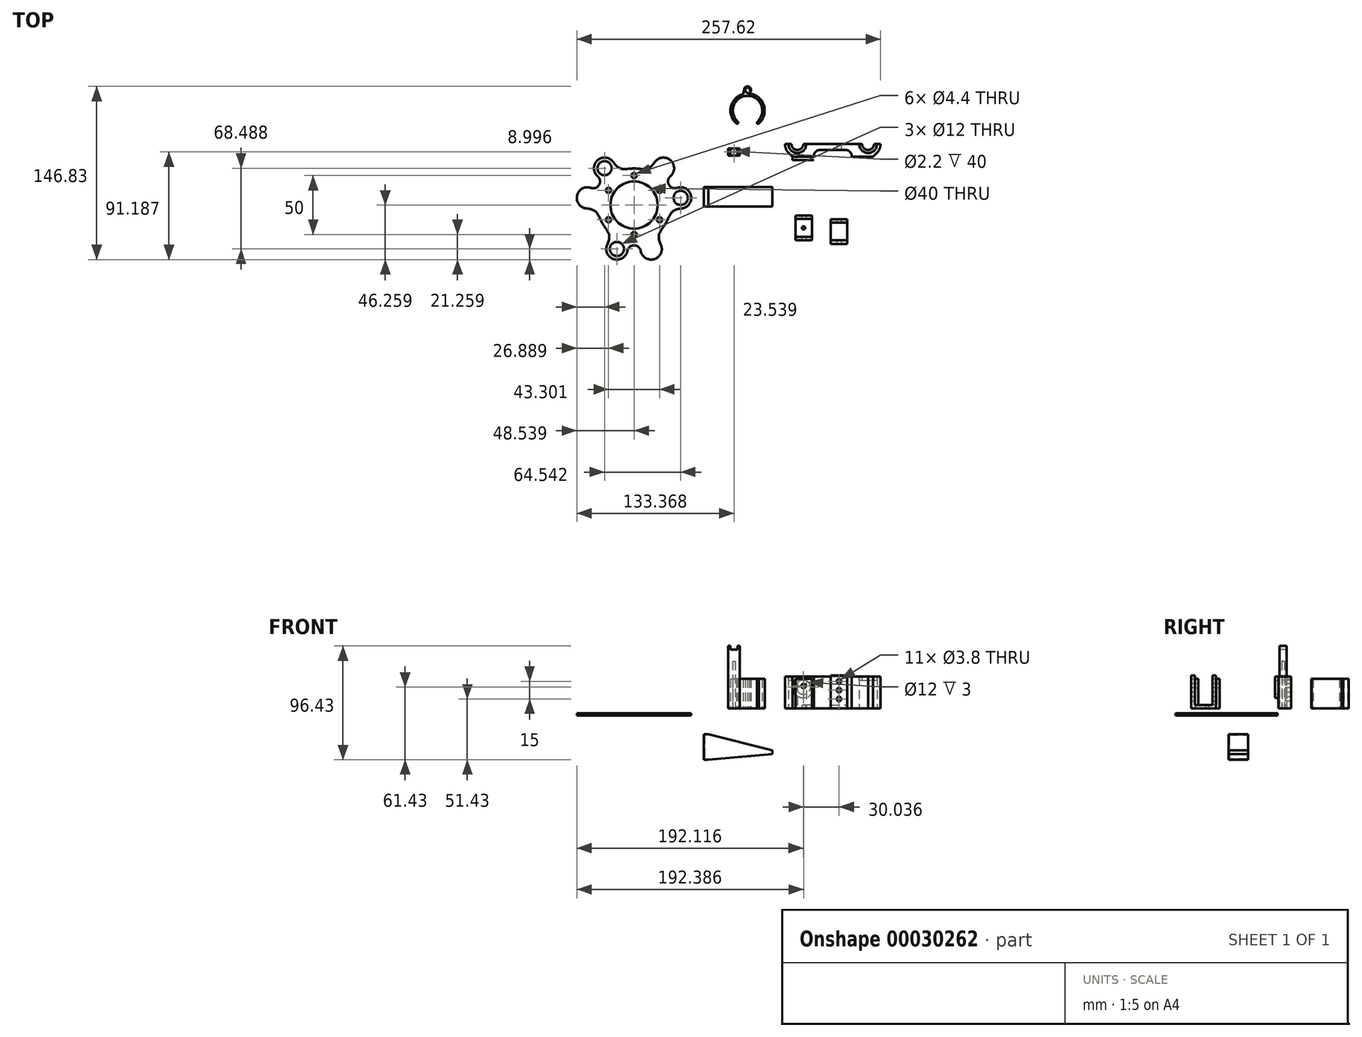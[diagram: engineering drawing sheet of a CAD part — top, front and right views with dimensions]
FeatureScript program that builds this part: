
annotation { "Feature Type Name" : "Feature", "Feature Type Description" : "" }
export const myFeature = defineFeature(function(context is Context, id is Id, definition is map)
    precondition{}
    {
        {
            var Q0;
            Q0=qCreatedBy(makeId("Top.planeOp"),FACE);
            var sketch = newSketch(context, id + "F0", { "sketchPlane" : qUnion([Q0])});
            skLineSegment(sketch, "E0.bottom", {"start": v(-40.53, 32.69) * mm, "end": v(-30.53, 32.69) * mm});
            skLineSegment(sketch, "E0.top", {"start": v(-40.53, 26.69) * mm, "end": v(-30.53, 26.69) * mm});
            skLineSegment(sketch, "E0.left", {"start": v(-40.53, 32.69) * mm, "end": v(-40.53, 26.69) * mm});
            skLineSegment(sketch, "E0.right", {"start": v(-30.53, 32.69) * mm, "end": v(-30.53, 26.69) * mm});
            skSolve(sketch);
        }
        {
            var Q0;
            Q0=makeQuery(id+"F0.imprint","IMPRINT",FACE,{"disambiguationData":[TD([[makeQuery(id+"F0.imprint","IMPRINT",EDGE,{"derivedFrom":sQuery(id+"F0.wireOp",EDGE,"E0.bottom")}),-1.0]])]});
            extrude(context, id + "F1", {"entities" : qUnion([Q0]), "depth" : 53 * mm});
        }
        {
            var Q0;
            Q0=makeQuery(id+"F1.opExtrude","CAP_FACE",FACE,{"disambiguationData":[OSD([sQuery(id+"F0.wireOp",EDGE,"E0.bottom"),sQuery(id+"F0.wireOp",EDGE,"E0.top"),sQuery(id+"F0.wireOp",EDGE,"E0.left"),sQuery(id+"F0.wireOp",EDGE,"E0.right")])],"isStart":false});
            var sketch = newSketch(context, id + "F2", { "sketchPlane" : qUnion([Q0])});
            skLineSegment(sketch, "E1", {"start": v(-38.53, 32.69) * mm, "end": v(-38.53, 26.69) * mm});
            skLineSegment(sketch, "E2", {"start": v(-32.53, 32.69) * mm, "end": v(-32.53, 26.69) * mm});
            skLineSegment(sketch, "E3", {"start": v(-38.53, 32.69) * mm, "end": v(-32.53, 32.69) * mm});
            skLineSegment(sketch, "E4", {"start": v(-38.53, 26.69) * mm, "end": v(-32.53, 26.69) * mm});
            skLineSegment(sketch, "E5", {"start": v(-38.53, 26.69) * mm, "end": v(-40.53, 26.69) * mm});
            skSolve(sketch);
        }
        {
            var Q0;
            Q0 = qSketchRegion(id + "F2", true);
            extrude(context, id + "F3", {"entities" : qUnion([Q0]), "operationType" : NewBodyOperationType.REMOVE, "oppositeDirection" : true, "depth" : 3 * mm});
        }
        {
            var Q0;
            Q0=makeQuery(id+"F1.opExtrude","CAP_FACE",FACE,{"disambiguationData":[OSD([sQuery(id+"F0.wireOp",EDGE,"E0.bottom"),sQuery(id+"F0.wireOp",EDGE,"E0.top"),sQuery(id+"F0.wireOp",EDGE,"E0.left"),sQuery(id+"F0.wireOp",EDGE,"E0.right")])],"isStart":true});
            var sketch = newSketch(context, id + "F4", { "sketchPlane" : qUnion([Q0])});
            skLineSegment(sketch, "E6", {"start": v(-35.53, -26.69) * mm, "end": v(-35.53, -32.69) * mm, "construction": true});
            skLineSegment(sketch, "E7", {"start": v(-40.53, -29.69) * mm, "end": v(-30.53, -29.69) * mm, "construction": true});
            skCircle(sketch, "E8", {"center": v(-35.53, -29.69) * mm, "radius": 1.1 * mm});
            skSolve(sketch);
        }
        {
            var Q0;
            Q0 = qSketchRegion(id + "F4", true);
            extrude(context, id + "F5", {"entities" : qUnion([Q0]), "operationType" : NewBodyOperationType.REMOVE, "oppositeDirection" : true, "depth" : 40 * mm});
        }
        {
            var Q0;
            Q0=qCreatedBy(makeId("Top.planeOp"),FACE);
            var sketch = newSketch(context, id + "F6", { "sketchPlane" : qUnion([Q0])});
            skLineSegment(sketch, "E9", {"start": v(-120.36, -15.24) * mm, "end": v(-120.36, 37.75) * mm, "construction": true});
            skLineSegment(sketch, "E10", {"start": v(-120.36, -15.24) * mm, "end": v(-160.35, -38.33) * mm, "construction": true});
            skLineSegment(sketch, "E11", {"start": v(-120.36, -15.24) * mm, "end": v(-52.6, -54.36) * mm, "construction": true});
            skLineSegment(sketch, "E12.0", {"start": v(-120.36, 13.63) * mm, "end": v(-172.85, -16.68) * mm, "construction": true});
            skLineSegment(sketch, "E12.1", {"start": v(-120.36, 13.63) * mm, "end": v(-40.1, -32.7) * mm, "construction": true});
            skLineSegment(sketch, "E13.0", {"start": v(-120.36, -44.1) * mm, "end": v(-147.85, -59.98) * mm, "construction": true});
            skLineSegment(sketch, "E13.1", {"start": v(-120.36, -44.1) * mm, "end": v(-65.1, -76) * mm, "construction": true});
            skLineSegment(sketch, "E14.0", {"start": v(-95.36, -0.8) * mm, "end": v(-95.36, 37.75) * mm, "construction": true});
            skLineSegment(sketch, "E15.0", {"start": v(-145.36, -0.8) * mm, "end": v(-145.36, 37.75) * mm, "construction": true});
            skCircle(sketch, "E16", {"center": v(-120.36, -15.24) * mm, "radius": 25 * mm, "construction": true});
            skCircle(sketch, "E17", {"center": v(-120.36, -15.24) * mm, "radius": 40 * mm, "construction": true});
            skCircle(sketch, "E18", {"center": v(-120.36, -15.24) * mm, "radius": 49 * mm, "construction": true});
            skCircle(sketch, "E19", {"center": v(-159.9, -9.2) * mm, "radius": 6 * mm});
            skCircle(sketch, "E20", {"center": v(-142.01, -27.74) * mm, "radius": 2.2 * mm});
            skLineSegment(sketch, "E21", {"start": v(-120.36, -15.24) * mm, "end": v(-145.36, -0.8) * mm, "construction": true});
            skLineSegment(sketch, "E22", {"start": v(-120.36, -15.24) * mm, "end": v(-120.36, -44.1) * mm, "construction": true});
            skCircle(sketch, "E23", {"center": v(-142.01, -2.74) * mm, "radius": 2.2 * mm});
            skCircle(sketch, "E24", {"center": v(-120.36, -15.24) * mm, "radius": 20 * mm});
            skArc(sketch, "E25", {"start": v(-156.92, -0.71) * mm, "mid": v(-168.74, -7.52) * mm, "end": v(-160.25, -18.2) * mm});
            skCircle(sketch, "E26", {"center": v(-120.36, -15.24) * mm, "radius": 31 * mm, "construction": true});
            skLineSegment(sketch, "E27", {"start": v(-145.36, -0.8) * mm, "end": v(-162.8, 9.26) * mm, "construction": true});
            skLineSegment(sketch, "E28", {"start": v(-120.36, -15.24) * mm, "end": v(-162.8, -39.74) * mm, "construction": true});
            skLineSegment(sketch, "E29", {"start": v(-120.36, -44.1) * mm, "end": v(-120.36, -64.24) * mm, "construction": true});
            skArc(sketch, "E30", {"start": v(-157.53, -0.46) * mm, "mid": v(-153.3, -0.78) * mm, "end": v(-149.98, 1.86) * mm});
            skLineSegment(sketch, "E31", {"start": v(-159.9, -9.2) * mm, "end": v(-120.36, -15.24) * mm, "construction": true});
            skLineSegment(sketch, "E32", {"start": v(-120.36, -15.24) * mm, "end": v(-145.36, 15.98) * mm, "construction": true});
            skFitSpline(sketch, "E33", {"points": [v(-160.25, -18.2) * mm, v(-147.2, -30.74) * mm], "startDerivative": vector(27.45, -3.14) * mm, "endDerivative": vector(12.8, -23.47) * mm});
            skPoint(sketch, "E34.MirrorCS.0.internal.orphan", {"position": v(-142.87, -48.31) * mm});
            skFitSpline(sketch, "E35.MirrorCS", {"points": [v(-142.87, -48.31) * mm, v(-147.2, -30.74) * mm], "startDerivative": vector(11, 25.34) * mm, "endDerivative": vector(-13.92, 22.82) * mm});
            skArc(sketch, "E36.MirrorCS", {"start": v(-126.06, -54.17) * mm, "mid": v(-137.86, -61) * mm, "end": v(-142.87, -48.31) * mm});
            skArc(sketch, "E37.MirrorCS", {"start": v(-126.14, -54.82) * mm, "mid": v(-124.3, -51) * mm, "end": v(-120.36, -49.44) * mm});
            skCircle(sketch, "E38.MirrorC", {"center": v(-134.9, -52.5) * mm, "radius": 6 * mm});
            skArc(sketch, "E39.MirrorCS", {"start": v(-151.75, 9.56) * mm, "mid": v(-149.35, 6.06) * mm, "end": v(-149.98, 1.86) * mm});
            skArc(sketch, "E40.MirrorCS", {"start": v(-151.22, 9.16) * mm, "mid": v(-151.24, 22.8) * mm, "end": v(-137.75, 20.78) * mm});
            skCircle(sketch, "E41.MirrorC", {"center": v(-145.36, 15.98) * mm, "radius": 6 * mm});
            skFitSpline(sketch, "E42.MirrorCS", {"points": [v(-137.75, 20.78) * mm, v(-120.36, 15.76) * mm], "startDerivative": vector(16.44, -22.2) * mm, "endDerivative": vector(26.72, 0.65) * mm});
            skCircle(sketch, "E43", {"center": v(-120.36, 9.76) * mm, "radius": 2.2 * mm});
            skCircle(sketch, "E44", {"center": v(-120.36, -40.24) * mm, "radius": 2.2 * mm});
            skFitSpline(sketch, "E45.MirrorCS", {"points": [v(-102.97, 20.78) * mm, v(-120.36, 15.76) * mm], "startDerivative": vector(-16.44, -22.2) * mm, "endDerivative": vector(-26.72, 0.65) * mm});
            skArc(sketch, "E46.MirrorCS", {"start": v(-89.5, 9.16) * mm, "mid": v(-89.48, 22.8) * mm, "end": v(-102.97, 20.78) * mm});
            skCircle(sketch, "E47.MirrorC", {"center": v(-95.36, 15.98) * mm, "radius": 6 * mm});
            skArc(sketch, "E48.MirrorCS", {"start": v(-88.97, 9.56) * mm, "mid": v(-91.37, 6.06) * mm, "end": v(-90.74, 1.86) * mm});
            skArc(sketch, "E49.MirrorCS", {"start": v(-83.2, -0.46) * mm, "mid": v(-87.42, -0.78) * mm, "end": v(-90.74, 1.86) * mm});
            skArc(sketch, "E50.MirrorCS", {"start": v(-83.8, -0.71) * mm, "mid": v(-71.98, -7.52) * mm, "end": v(-80.47, -18.2) * mm});
            skCircle(sketch, "E51.MirrorC", {"center": v(-80.82, -9.2) * mm, "radius": 6 * mm});
            skFitSpline(sketch, "E52.MirrorCS", {"points": [v(-80.47, -18.2) * mm, v(-93.51, -30.74) * mm], "startDerivative": vector(-27.45, -3.14) * mm, "endDerivative": vector(-12.8, -23.47) * mm});
            skCircle(sketch, "E53.MirrorC", {"center": v(-98.71, -27.74) * mm, "radius": 2.2 * mm});
            skCircle(sketch, "E54.MirrorC", {"center": v(-98.71, -2.74) * mm, "radius": 2.2 * mm});
            skFitSpline(sketch, "E55.MirrorCS", {"points": [v(-97.86, -48.31) * mm, v(-93.51, -30.74) * mm], "startDerivative": vector(-11, 25.34) * mm, "endDerivative": vector(13.92, 22.82) * mm});
            skArc(sketch, "E56.MirrorCS", {"start": v(-114.66, -54.17) * mm, "mid": v(-102.86, -61) * mm, "end": v(-97.86, -48.31) * mm});
            skCircle(sketch, "E57.MirrorC", {"center": v(-105.82, -52.5) * mm, "radius": 6 * mm});
            skArc(sketch, "E58.MirrorCS", {"start": v(-114.58, -54.82) * mm, "mid": v(-116.41, -51) * mm, "end": v(-120.36, -49.44) * mm});
            skSolve(sketch);
        }
        {
            var Q0;
            Q0=makeQuery(id+"F6.imprint","IMPRINT",FACE,{"disambiguationData":[TD([[makeQuery(id+"F6.imprint","IMPRINT",EDGE,{"derivedFrom":sQuery(id+"F6.wireOp",EDGE,"E19")}),-1.0]])]});
            var Q1;
            Q1=makeQuery(id+"F6.imprint","IMPRINT",FACE,{"disambiguationData":[TD([[makeQuery(id+"F6.imprint","IMPRINT",EDGE,{"derivedFrom":sQuery(id+"F6.wireOp",EDGE,"E19")}),1.0]])]});
            var Q2;
            Q2=makeQuery(id+"F6.imprint","IMPRINT",FACE,{"disambiguationData":[TD([[makeQuery(id+"F6.imprint","IMPRINT",EDGE,{"derivedFrom":sQuery(id+"F6.wireOp",EDGE,"E41.MirrorC")}),-1.0]])]});
            var Q3;
            Q3=makeQuery(id+"F6.imprint","IMPRINT",FACE,{"disambiguationData":[TD([[makeQuery(id+"F6.imprint","IMPRINT",EDGE,{"derivedFrom":sQuery(id+"F6.wireOp",EDGE,"E47.MirrorC")}),1.0]])]});
            var Q4;
            Q4=makeQuery(id+"F6.imprint","IMPRINT",FACE,{"disambiguationData":[TD([[makeQuery(id+"F6.imprint","IMPRINT",EDGE,{"derivedFrom":sQuery(id+"F6.wireOp",EDGE,"E51.MirrorC")}),-1.0]])]});
            var Q5;
            Q5=makeQuery(id+"F6.imprint","IMPRINT",FACE,{"disambiguationData":[TD([[makeQuery(id+"F6.imprint","IMPRINT",EDGE,{"derivedFrom":sQuery(id+"F6.wireOp",EDGE,"E57.MirrorC")}),1.0]])]});
            var Q6;
            Q6=makeQuery(id+"F6.imprint","IMPRINT",FACE,{"disambiguationData":[TD([[makeQuery(id+"F6.imprint","IMPRINT",EDGE,{"derivedFrom":sQuery(id+"F6.wireOp",EDGE,"E38.MirrorC")}),-1.0]])]});
            var Q7;
            Q7=sQuery(id+"F6.wireOp",EDGE,"E33");
            var Q8;
            Q8=sQuery(id+"F6.wireOp",EDGE,"E25");
            var Q9;
            Q9=sQuery(id+"F6.wireOp",EDGE,"E19");
            var Q10;
            Q10=sQuery(id+"F6.wireOp",EDGE,"E41.MirrorC");
            var Q11;
            Q11=sQuery(id+"F6.wireOp",EDGE,"E40.MirrorCS");
            var Q12;
            Q12=sQuery(id+"F6.wireOp",EDGE,"E30");
            var Q13;
            Q13=sQuery(id+"F6.wireOp",EDGE,"E39.MirrorCS");
            var Q14;
            Q14=sQuery(id+"F6.wireOp",EDGE,"E35.MirrorCS");
            var Q15;
            Q15=sQuery(id+"F6.wireOp",EDGE,"E36.MirrorCS");
            var Q16;
            Q16=sQuery(id+"F6.wireOp",EDGE,"E37.MirrorCS");
            var Q17;
            Q17=sQuery(id+"F6.wireOp",EDGE,"E58.MirrorCS");
            var Q18;
            Q18=sQuery(id+"F6.wireOp",EDGE,"E56.MirrorCS");
            var Q19;
            Q19=sQuery(id+"F6.wireOp",EDGE,"E55.MirrorCS");
            var Q20;
            Q20=sQuery(id+"F6.wireOp",EDGE,"E52.MirrorCS");
            var Q21;
            Q21=sQuery(id+"F6.wireOp",EDGE,"E50.MirrorCS");
            var Q22;
            Q22=sQuery(id+"F6.wireOp",EDGE,"E49.MirrorCS");
            var Q23;
            Q23=sQuery(id+"F6.wireOp",EDGE,"E48.MirrorCS");
            var Q24;
            Q24=sQuery(id+"F6.wireOp",EDGE,"E46.MirrorCS");
            var Q25;
            Q25=sQuery(id+"F6.wireOp",EDGE,"E45.MirrorCS");
            var Q26;
            Q26=sQuery(id+"F6.wireOp",EDGE,"E42.MirrorCS");
            var Q27;
            Q27=sQuery(id+"F6.wireOp",EDGE,"E47.MirrorC");
            var Q28;
            Q28=sQuery(id+"F6.wireOp",EDGE,"E51.MirrorC");
            var Q29;
            Q29=sQuery(id+"F6.wireOp",EDGE,"E57.MirrorC");
            var Q30;
            Q30=sQuery(id+"F6.wireOp",EDGE,"E38.MirrorC");
            extrude(context, id + "F7", {"entities" : qUnion([Q0, Q1, Q2, Q3, Q4, Q5, Q6]), "surfaceEntities" : qUnion([Q7, Q8, Q9, Q10, Q11, Q12, Q13, Q14, Q15, Q16, Q17, Q18, Q19, Q20, Q21, Q22, Q23, Q24, Q25, Q26, Q27, Q28, Q29, Q30]), "oppositeDirection" : true, "depth" : 6 * mm});
        }
        {
            var Q0;
            Q0=makeQuery(id+"F6.imprint","IMPRINT",FACE,{"disambiguationData":[TD([[makeQuery(id+"F6.imprint","IMPRINT",EDGE,{"derivedFrom":sQuery(id+"F6.wireOp",EDGE,"E19")}),1.0]])]});
            var Q1;
            Q1=makeQuery(id+"F6.imprint","IMPRINT",FACE,{"disambiguationData":[TD([[makeQuery(id+"F6.imprint","IMPRINT",EDGE,{"derivedFrom":sQuery(id+"F6.wireOp",EDGE,"E41.MirrorC")}),-1.0]])]});
            var Q2;
            Q2=makeQuery(id+"F6.imprint","IMPRINT",FACE,{"disambiguationData":[TD([[makeQuery(id+"F6.imprint","IMPRINT",EDGE,{"derivedFrom":sQuery(id+"F6.wireOp",EDGE,"E47.MirrorC")}),1.0]])]});
            var Q3;
            Q3=makeQuery(id+"F6.imprint","IMPRINT",FACE,{"disambiguationData":[TD([[makeQuery(id+"F6.imprint","IMPRINT",EDGE,{"derivedFrom":sQuery(id+"F6.wireOp",EDGE,"E51.MirrorC")}),-1.0]])]});
            var Q4;
            Q4=makeQuery(id+"F6.imprint","IMPRINT",FACE,{"disambiguationData":[TD([[makeQuery(id+"F6.imprint","IMPRINT",EDGE,{"derivedFrom":sQuery(id+"F6.wireOp",EDGE,"E57.MirrorC")}),1.0]])]});
            var Q5;
            Q5=makeQuery(id+"F6.imprint","IMPRINT",FACE,{"disambiguationData":[TD([[makeQuery(id+"F6.imprint","IMPRINT",EDGE,{"derivedFrom":sQuery(id+"F6.wireOp",EDGE,"E38.MirrorC")}),-1.0]])]});
            extrude(context, id + "F8", {"entities" : qUnion([Q0, Q1, Q2, Q3, Q4, Q5]), "operationType" : NewBodyOperationType.REMOVE, "oppositeDirection" : true, "depth" : 4 * mm});
        }
        {
            var Q0;
            Q0=qCreatedBy(makeId("Top.planeOp"),FACE);
            var sketch = newSketch(context, id + "F9", { "sketchPlane" : qUnion([Q0])});
            skArc(sketch, "E59", {"start": v(10.72, 36.36) * mm, "mid": v(18.22, 28.86) * mm, "end": v(25.72, 36.36) * mm});
            skLineSegment(sketch, "E60", {"start": v(18.22, 36.36) * mm, "end": v(18.22, 71.19) * mm, "construction": true});
            skLineSegment(sketch, "E61", {"start": v(18.22, 36.36) * mm, "end": v(78.22, 36.36) * mm, "construction": true});
            skLineSegment(sketch, "E62.trimOffspring", {"start": v(25.72, 36.36) * mm, "end": v(70.72, 36.36) * mm});
            skArc(sketch, "E63.2", {"start": v(7.72, 36.36) * mm, "mid": v(8.62, 32.1) * mm, "end": v(11.17, 28.58) * mm});
            skLineSegment(sketch, "E64", {"start": v(7.72, 36.36) * mm, "end": v(10.72, 36.36) * mm});
            skLineSegment(sketch, "E65", {"start": v(48.22, 36.36) * mm, "end": v(48.22, 25.86) * mm, "construction": true});
            skLineSegment(sketch, "E66", {"start": v(23.22, 30.77) * mm, "end": v(23.22, 17.71) * mm, "construction": true});
            skLineSegment(sketch, "E67", {"start": v(14.22, 30.02) * mm, "end": v(14.22, 16.99) * mm, "construction": true});
            skLineSegment(sketch, "E68", {"start": v(18.33, 25.86) * mm, "end": v(32.22, 25.86) * mm});
            skLineSegment(sketch, "E69", {"start": v(48.22, 36.36) * mm, "end": v(48.22, 51.42) * mm, "construction": true});
            skLineSegment(sketch, "E70", {"start": v(18.33, 25.86) * mm, "end": v(14.22, 25.82) * mm});
            skLineSegment(sketch, "E71", {"start": v(14.22, 25.82) * mm, "end": v(11.17, 28.58) * mm});
            skLineSegment(sketch, "E72.MirrorCS", {"start": v(78.1, 25.86) * mm, "end": v(64.22, 25.86) * mm});
            skArc(sketch, "E73.MirrorCS", {"start": v(85.72, 36.36) * mm, "mid": v(78.22, 28.86) * mm, "end": v(70.72, 36.36) * mm});
            skLineSegment(sketch, "E74.MirrorCS", {"start": v(88.72, 36.36) * mm, "end": v(85.72, 36.36) * mm});
            skArc(sketch, "E75.MirrorCS", {"start": v(88.72, 36.36) * mm, "mid": v(87.81, 32.1) * mm, "end": v(85.27, 28.58) * mm});
            skLineSegment(sketch, "E76.MirrorCS", {"start": v(82.22, 25.82) * mm, "end": v(85.27, 28.58) * mm});
            skLineSegment(sketch, "E77.MirrorCS", {"start": v(78.1, 25.86) * mm, "end": v(82.22, 25.82) * mm});
            skLineSegment(sketch, "E78", {"start": v(32.22, 36.36) * mm, "end": v(32.22, 7.75) * mm, "construction": true});
            skLineSegment(sketch, "E79", {"start": v(37.22, 31.36) * mm, "end": v(48.22, 31.36) * mm});
            skLineSegment(sketch, "E80", {"start": v(32.22, 25.86) * mm, "end": v(32.22, 26.36) * mm});
            skLineSegment(sketch, "E81.MirrorCS", {"start": v(59.22, 31.36) * mm, "end": v(48.22, 31.36) * mm});
            skLineSegment(sketch, "E82.MirrorCS", {"start": v(64.22, 25.86) * mm, "end": v(64.22, 26.36) * mm});
            skPoint(sketch, "E83.orphan", {"position": v(48.22, 25.86) * mm});
            skPoint(sketch, "E84.visualSharp", {"position": v(32.22, 31.36) * mm});
            skArc(sketch, "E84.filletArc", {"start": v(37.22, 31.36) * mm, "mid": v(33.68, 29.9) * mm, "end": v(32.22, 26.36) * mm});
            skArc(sketch, "E85.MirrorCS", {"start": v(59.22, 31.36) * mm, "mid": v(62.75, 29.9) * mm, "end": v(64.22, 26.36) * mm});
            skPoint(sketch, "E86.orphan", {"position": v(64.22, 31.36) * mm});
            skSolve(sketch);
        }
        {
            var Q0;
            Q0 = qSketchRegion(id + "F9", true);
            extrude(context, id + "F10", {"entities" : qUnion([Q0]), "depth" : 27 * mm});
        }
        {
            var Q0;
            Q0=makeQuery(id+"F10.opExtrude","SWEPT_FACE",FACE,{"disambiguationData":[OSD([sQuery(id+"F9.wireOp",EDGE,"E68")])]});
            var sketch = newSketch(context, id + "F11", { "sketchPlane" : qUnion([Q0])});
            skLineSegment(sketch, "E87", {"start": v(23.22, 27) * mm, "end": v(23.22, 0) * mm, "construction": true});
            skLineSegment(sketch, "E88", {"start": v(23.22, 18) * mm, "end": v(48.22, 18) * mm, "construction": true});
            skCircle(sketch, "E89", {"center": v(23.22, 18) * mm, "radius": 6 * mm});
            skCircle(sketch, "E90", {"center": v(23.22, 18) * mm, "radius": 9 * mm});
            skCircle(sketch, "E91.MirrorC", {"center": v(73.22, 18) * mm, "radius": 9 * mm});
            skCircle(sketch, "E92.MirrorC", {"center": v(73.22, 18) * mm, "radius": 6 * mm});
            skSolve(sketch);
        }
        {
            var Q0;
            {var subQ0=makeQuery(id+"F10.opExtrude","SWEPT_EDGE",EDGE,{"disambiguationData":[OSD([sQuery(id+"F9.wireOp",EDGE,"E68"),sQuery(id+"F9.wireOp",EDGE,"E70")])]});var subQ1=sQuery(id+"F11.wireOp",EDGE,"E89");var subQ5=makeQuery(id+"F11.imprint","INTERSECT",VERTEX,{"disambiguationData":[OD(0.0)],"derivedFrom":[subQ0,subQ1]});Q0=makeQuery(id+"F11.imprint","IMPRINT",FACE,{"disambiguationData":[TD([[makeQuery(id+"F11.imprint","IMPRINT",EDGE,{"disambiguationData":[TD([[subQ5,-1.0]])],"derivedFrom":subQ1}),-1.0]])]});}
            var Q1;
            {var subQ0=sQuery(id+"F9.wireOp",EDGE,"E68");var subQ4=sQuery(id+"F11.wireOp",EDGE,"E90");var subQ8=makeQuery(id+"F11.imprint","INTERSECT",VERTEX,{"derivedFrom":[makeQuery(id+"F10.opExtrude","CAP_EDGE",EDGE,{"disambiguationData":[OSD([subQ0])],"isStart":false}),subQ4]});Q1=makeQuery(id+"F11.imprint","IMPRINT",FACE,{"disambiguationData":[TD([[makeQuery(id+"F11.imprint","IMPRINT",EDGE,{"disambiguationData":[TD([[subQ8,-1.0]])],"derivedFrom":subQ4}),1.0]])]});}
            var Q2;
            Q2=makeQuery(id+"F11.imprint","IMPRINT",FACE,{"disambiguationData":[TD([[makeQuery(id+"F11.imprint","IMPRINT",EDGE,{"derivedFrom":sQuery(id+"F11.wireOp",EDGE,"E91.MirrorC")}),-1.0]])]});
            extrude(context, id + "F12", {"entities" : qUnion([Q0, Q1, Q2]), "operationType" : NewBodyOperationType.ADD, "depth" : 3 * mm});
        }
        {
            var Q0;
            Q0=makeQuery(id+"F10.opExtrude","CAP_FACE",FACE,{"disambiguationData":[OSD([sQuery(id+"F9.wireOp",EDGE,"E59"),sQuery(id+"F9.wireOp",EDGE,"E62.trimOffspring"),sQuery(id+"F9.wireOp",EDGE,"E63.2"),sQuery(id+"F9.wireOp",EDGE,"E64"),sQuery(id+"F9.wireOp",EDGE,"E68"),sQuery(id+"F9.wireOp",EDGE,"E70"),sQuery(id+"F9.wireOp",EDGE,"E71"),sQuery(id+"F9.wireOp",EDGE,"E72.MirrorCS"),sQuery(id+"F9.wireOp",EDGE,"E73.MirrorCS"),sQuery(id+"F9.wireOp",EDGE,"E74.MirrorCS"),sQuery(id+"F9.wireOp",EDGE,"E75.MirrorCS"),sQuery(id+"F9.wireOp",EDGE,"E76.MirrorCS"),sQuery(id+"F9.wireOp",EDGE,"E77.MirrorCS")])],"isStart":false});
            var sketch = newSketch(context, id + "F13", { "sketchPlane" : qUnion([Q0])});
            skLineSegment(sketch, "E93", {"start": v(10.72, 36.36) * mm, "end": v(13.22, 36.36) * mm});
            skLineSegment(sketch, "E94", {"start": v(25.72, 36.36) * mm, "end": v(73.22, 36.36) * mm});
            skArc(sketch, "E95", {"start": v(13.22, 36.36) * mm, "mid": v(18.22, 31.36) * mm, "end": v(23.22, 36.36) * mm});
            skArc(sketch, "E96", {"start": v(73.22, 36.36) * mm, "mid": v(78.22, 31.36) * mm, "end": v(83.22, 36.36) * mm});
            skLineSegment(sketch, "E97.trimOffspring", {"start": v(83.22, 36.36) * mm, "end": v(85.72, 36.36) * mm});
            skLineSegment(sketch, "E98.trimOffspring", {"start": v(23.22, 36.36) * mm, "end": v(25.72, 36.36) * mm});
            skSolve(sketch);
        }
        {
            var Q0;
            {var subQ0=sQuery(id+"F13.wireOp",EDGE,"E96");Q0=makeQuery(id+"F13.imprint","IMPRINT",FACE,{"disambiguationData":[TD([[makeQuery(id+"F13.imprint","IMPRINT",EDGE,{"derivedFrom":subQ0}),-1.0]])]});}
            var Q1;
            Q1=makeQuery(id+"F13.imprint","IMPRINT",FACE,{"disambiguationData":[TD([[makeQuery(id+"F13.imprint","IMPRINT",EDGE,{"derivedFrom":sQuery(id+"F13.wireOp",EDGE,"E93")}),-1.0]])]});
            extrude(context, id + "F14", {"entities" : qUnion([Q0, Q1]), "oppositeDirection" : true, "depth" : 3 * mm});
        }
        {
            var Q0;
            Q0=qCreatedBy(makeId("Top.planeOp"),FACE);
            var sketch = newSketch(context, id + "F15", { "sketchPlane" : qUnion([Q0])});
            skLineSegment(sketch, "E99.bottom", {"start": v(16.49, -24.15) * mm, "end": v(30.49, -24.15) * mm});
            skLineSegment(sketch, "E99.top", {"start": v(16.49, -45.15) * mm, "end": v(30.49, -45.15) * mm});
            skLineSegment(sketch, "E99.left", {"start": v(16.49, -24.15) * mm, "end": v(16.49, -45.15) * mm});
            skLineSegment(sketch, "E99.right", {"start": v(30.49, -24.15) * mm, "end": v(30.49, -45.15) * mm});
            skSolve(sketch);
        }
        {
            var Q0;
            Q0 = qSketchRegion(id + "F15", true);
            extrude(context, id + "F16", {"entities" : qUnion([Q0]), "depth" : 25 * mm});
        }
        {
            var Q0;
            Q0=makeQuery(id+"F16.opExtrude","SWEPT_FACE",FACE,{"disambiguationData":[OSD([sQuery(id+"F15.wireOp",EDGE,"E99.left")])]});
            var sketch = newSketch(context, id + "F17", { "sketchPlane" : qUnion([Q0])});
            skLineSegment(sketch, "E100", {"start": v(34.65, 0) * mm, "end": v(34.65, 25) * mm, "construction": true});
            skLineSegment(sketch, "E101", {"start": v(27.15, 25) * mm, "end": v(27.15, 3) * mm});
            skLineSegment(sketch, "E102", {"start": v(27.15, 3) * mm, "end": v(34.65, 3) * mm});
            skLineSegment(sketch, "E103.MirrorCS", {"start": v(42.15, 25) * mm, "end": v(42.15, 3) * mm});
            skLineSegment(sketch, "E104.MirrorCS", {"start": v(42.15, 3) * mm, "end": v(34.65, 3) * mm});
            skSolve(sketch);
        }
        {
            var Q0;
            Q0 = qSketchRegion(id + "F17", true);
            var Q1;
            {var subQ2=sQuery(id+"F17.wireOp",EDGE,"E101");Q1=makeQuery(id+"F17.imprint","IMPRINT",FACE,{"disambiguationData":[TD([[makeQuery(id+"F17.imprint","IMPRINT",EDGE,{"derivedFrom":subQ2}),1.0]])]});}
            extrude(context, id + "F18", {"entities" : qUnion([Q0, Q1]), "operationType" : NewBodyOperationType.REMOVE, "endBound" : BoundingType.UP_TO_NEXT, "oppositeDirection" : true, "depth" : 25 * mm});
        }
        {
            var Q0;
            Q0=makeQuery(id+"F16.opExtrude","SWEPT_FACE",FACE,{"disambiguationData":[OSD([sQuery(id+"F15.wireOp",EDGE,"E99.top")])]});
            var sketch = newSketch(context, id + "F19", { "sketchPlane" : qUnion([Q0])});
            skLineSegment(sketch, "E105", {"start": v(30.49, 19) * mm, "end": v(16.49, 19) * mm, "construction": true});
            skCircle(sketch, "E106", {"center": v(23.49, 19) * mm, "radius": 1.9 * mm});
            skSolve(sketch);
        }
        {
            var Q0;
            Q0 = qSketchRegion(id + "F19", true);
            extrude(context, id + "F20", {"entities" : qUnion([Q0]), "operationType" : NewBodyOperationType.REMOVE, "oppositeDirection" : true, "depth" : 35.06 * mm});
        }
        {
            var Q0;
            Q0=makeQuery(id+"F16.opExtrude","CAP_FACE",FACE,{"disambiguationData":[OSD([sQuery(id+"F15.wireOp",EDGE,"E99.bottom"),sQuery(id+"F15.wireOp",EDGE,"E99.top"),sQuery(id+"F15.wireOp",EDGE,"E99.left"),sQuery(id+"F15.wireOp",EDGE,"E99.right")])],"isStart":true});
            var sketch = newSketch(context, id + "F21", { "sketchPlane" : qUnion([Q0])});
            skCircle(sketch, "E107", {"center": v(23.49, 34.65) * mm, "radius": 1.35 * mm});
            skPoint(sketch, "E107.centerSnap0", {"position": v(23.49, 24.15) * mm});
            skPoint(sketch, "E107.centerSnap1", {"position": v(30.49, 34.65) * mm});
            skSolve(sketch);
        }
        {
            var Q0;
            Q0 = qSketchRegion(id + "F21", true);
            extrude(context, id + "F22", {"entities" : qUnion([Q0]), "operationType" : NewBodyOperationType.REMOVE, "endBound" : BoundingType.UP_TO_NEXT, "oppositeDirection" : true, "depth" : 25 * mm});
        }
        {
            var Q0;
            Q0=qCreatedBy(makeId("Top.planeOp"),FACE);
            var sketch = newSketch(context, id + "F23", { "sketchPlane" : qUnion([Q0])});
            skLineSegment(sketch, "E108.bottom", {"start": v(46.52, -27.22) * mm, "end": v(60.52, -27.22) * mm});
            skLineSegment(sketch, "E108.top", {"start": v(46.52, -48.22) * mm, "end": v(60.52, -48.22) * mm});
            skLineSegment(sketch, "E108.left", {"start": v(46.52, -27.22) * mm, "end": v(46.52, -48.22) * mm});
            skLineSegment(sketch, "E108.right", {"start": v(60.52, -27.22) * mm, "end": v(60.52, -48.22) * mm});
            skSolve(sketch);
        }
        {
            var Q0;
            Q0 = qSketchRegion(id + "F23", true);
            extrude(context, id + "F24", {"entities" : qUnion([Q0]), "depth" : 28 * mm});
        }
        {
            var Q0;
            Q0=makeQuery(id+"F24.opExtrude","SWEPT_FACE",FACE,{"disambiguationData":[OSD([sQuery(id+"F23.wireOp",EDGE,"E108.right")])]});
            var sketch = newSketch(context, id + "F25", { "sketchPlane" : qUnion([Q0])});
            skLineSegment(sketch, "E109.bottom", {"start": v(-45.22, 28) * mm, "end": v(-30.22, 28) * mm});
            skLineSegment(sketch, "E109.top", {"start": v(-45.22, 3) * mm, "end": v(-30.22, 3) * mm});
            skLineSegment(sketch, "E109.left", {"start": v(-45.22, 28) * mm, "end": v(-45.22, 3) * mm});
            skLineSegment(sketch, "E109.right", {"start": v(-30.22, 28) * mm, "end": v(-30.22, 3) * mm});
            skSolve(sketch);
        }
        {
            var Q0;
            Q0 = qSketchRegion(id + "F25", true);
            extrude(context, id + "F26", {"entities" : qUnion([Q0]), "operationType" : NewBodyOperationType.REMOVE, "endBound" : BoundingType.UP_TO_NEXT, "oppositeDirection" : true, "depth" : 25 * mm});
        }
        {
            var Q0;
            Q0=makeQuery(id+"F24.opExtrude","SWEPT_FACE",FACE,{"disambiguationData":[OSD([sQuery(id+"F23.wireOp",EDGE,"E108.top")])]});
            var sketch = newSketch(context, id + "F27", { "sketchPlane" : qUnion([Q0])});
            skLineSegment(sketch, "E110", {"start": v(46.52, 23) * mm, "end": v(60.52, 23) * mm, "construction": true});
            skCircle(sketch, "E111", {"center": v(53.52, 23) * mm, "radius": 1.9 * mm});
            skLineSegment(sketch, "E112", {"start": v(46.52, 8) * mm, "end": v(60.52, 8) * mm, "construction": true});
            skCircle(sketch, "E113", {"center": v(53.52, 8) * mm, "radius": 1.9 * mm});
            skLineSegment(sketch, "E114", {"start": v(46.52, 15.5) * mm, "end": v(60.52, 15.5) * mm, "construction": true});
            skCircle(sketch, "E115", {"center": v(53.52, 15.5) * mm, "radius": 1.9 * mm});
            skSolve(sketch);
        }
        {
            var Q0;
            Q0 = qSketchRegion(id + "F27", true);
            extrude(context, id + "F28", {"entities" : qUnion([Q0]), "operationType" : NewBodyOperationType.REMOVE, "endBound" : BoundingType.THROUGH_ALL, "oppositeDirection" : true, "depth" : 25 * mm});
        }
        {
            var Q0;
            Q0=qCreatedBy(makeId("Front.planeOp"),FACE);
            var sketch = newSketch(context, id + "F29", { "sketchPlane" : qUnion([Q0])});
            skLineSegment(sketch, "E116", {"start": v(-61.2, -43.43) * mm, "end": v(-57.2, -43.43) * mm});
            skLineSegment(sketch, "E117", {"start": v(-57.2, -21.83) * mm, "end": v(-61.2, -21.83) * mm});
            skLineSegment(sketch, "E118", {"start": v(-61.2, -21.83) * mm, "end": v(-61.2, -43.43) * mm});
            skLineSegment(sketch, "E119", {"start": v(-57.2, -43.43) * mm, "end": v(-3.2, -38.55) * mm});
            skLineSegment(sketch, "E120", {"start": v(-3.2, -38.55) * mm, "end": v(-3.2, -35.55) * mm});
            skLineSegment(sketch, "E121", {"start": v(-3.2, -35.55) * mm, "end": v(-57.2, -21.83) * mm});
            skLineSegment(sketch, "E122", {"start": v(-3.2, -37.05) * mm, "end": v(-61.2, -37.05) * mm, "construction": true});
            skSolve(sketch);
        }
        {
            var Q0;
            Q0 = qSketchRegion(id + "F29", true);
            extrude(context, id + "F30", {"entities" : qUnion([Q0]), "depth" : 16.4 * mm});
        }
        {
            var Q0;
            Q0=makeQuery(id+"F30.opExtrude","SWEPT_FACE",FACE,{"disambiguationData":[OSD([sQuery(id+"F29.wireOp",EDGE,"E118")])]});
            var sketch = newSketch(context, id + "F31", { "sketchPlane" : qUnion([Q0])});
            skLineSegment(sketch, "E123.0", {"start": v(0.7, -22.53) * mm, "end": v(0.7, -42.73) * mm});
            skLineSegment(sketch, "E123.1", {"start": v(15.7, -22.53) * mm, "end": v(0.7, -22.53) * mm});
            skLineSegment(sketch, "E123.2", {"start": v(15.7, -42.73) * mm, "end": v(15.7, -22.53) * mm});
            skLineSegment(sketch, "E123.3", {"start": v(0.7, -42.73) * mm, "end": v(15.7, -42.73) * mm});
            skSolve(sketch);
        }
        {
            var Q0;
            Q0 = qSketchRegion(id + "F31", true);
            extrude(context, id + "F32", {"entities" : qUnion([Q0]), "operationType" : NewBodyOperationType.REMOVE, "oppositeDirection" : true, "depth" : .7 * mm});
        }
        {
            var Q0;
            Q0=qCreatedBy(makeId("Top.planeOp"),FACE);
            var sketch = newSketch(context, id + "F33", { "sketchPlane" : qUnion([Q0])});
            skArc(sketch, "E124", {"start": v(-15.9, 55.35) * mm, "mid": v(-24.05, 77.33) * mm, "end": v(-32.2, 55.35) * mm});
            skArc(sketch, "E125.0", {"start": v(-27.94, 78.8) * mm, "mid": v(-38.2, 67.99) * mm, "end": v(-33.5, 53.83) * mm});
            skLineSegment(sketch, "E126", {"start": v(-24.05, 64.83) * mm, "end": v(-24.05, 91.99) * mm, "construction": true});
            skArc(sketch, "E127", {"start": v(-21.63, 80.57) * mm, "mid": v(-22.81, 85.06) * mm, "end": v(-26.98, 83) * mm});
            skArc(sketch, "E128", {"start": v(-22.44, 81.16) * mm, "mid": v(-24.16, 84.33) * mm, "end": v(-25.55, 81) * mm});
            skLineSegment(sketch, "E129", {"start": v(-27.94, 78.8) * mm, "end": v(-26.98, 83) * mm});
            skLineSegment(sketch, "E130", {"start": v(-22.44, 81.16) * mm, "end": v(-21.63, 80.57) * mm});
            skLineSegment(sketch, "E131", {"start": v(-24.05, 79.33) * mm, "end": v(-25.55, 81) * mm});
            skArc(sketch, "E132", {"start": v(-33.5, 53.83) * mm, "mid": v(-32.16, 54) * mm, "end": v(-32.2, 55.35) * mm});
            skArc(sketch, "E133.MirrorCS", {"start": v(-14.6, 53.83) * mm, "mid": v(-15.95, 54) * mm, "end": v(-15.9, 55.35) * mm});
            skArc(sketch, "E134.trimOffspring", {"start": v(-14.6, 53.83) * mm, "mid": v(-10.46, 69.87) * mm, "end": v(-24.05, 79.33) * mm});
            skSolve(sketch);
        }
        {
            var Q0;
            Q0=makeQuery(id+"F33.imprint","IMPRINT",FACE,{"disambiguationData":[TD([[makeQuery(id+"F33.imprint","IMPRINT",EDGE,{"derivedFrom":sQuery(id+"F33.wireOp",EDGE,"E124")}),-1.0]])]});
            extrude(context, id + "F34", {"entities" : qUnion([Q0]), "depth" : 25 * mm});
        }
    });
